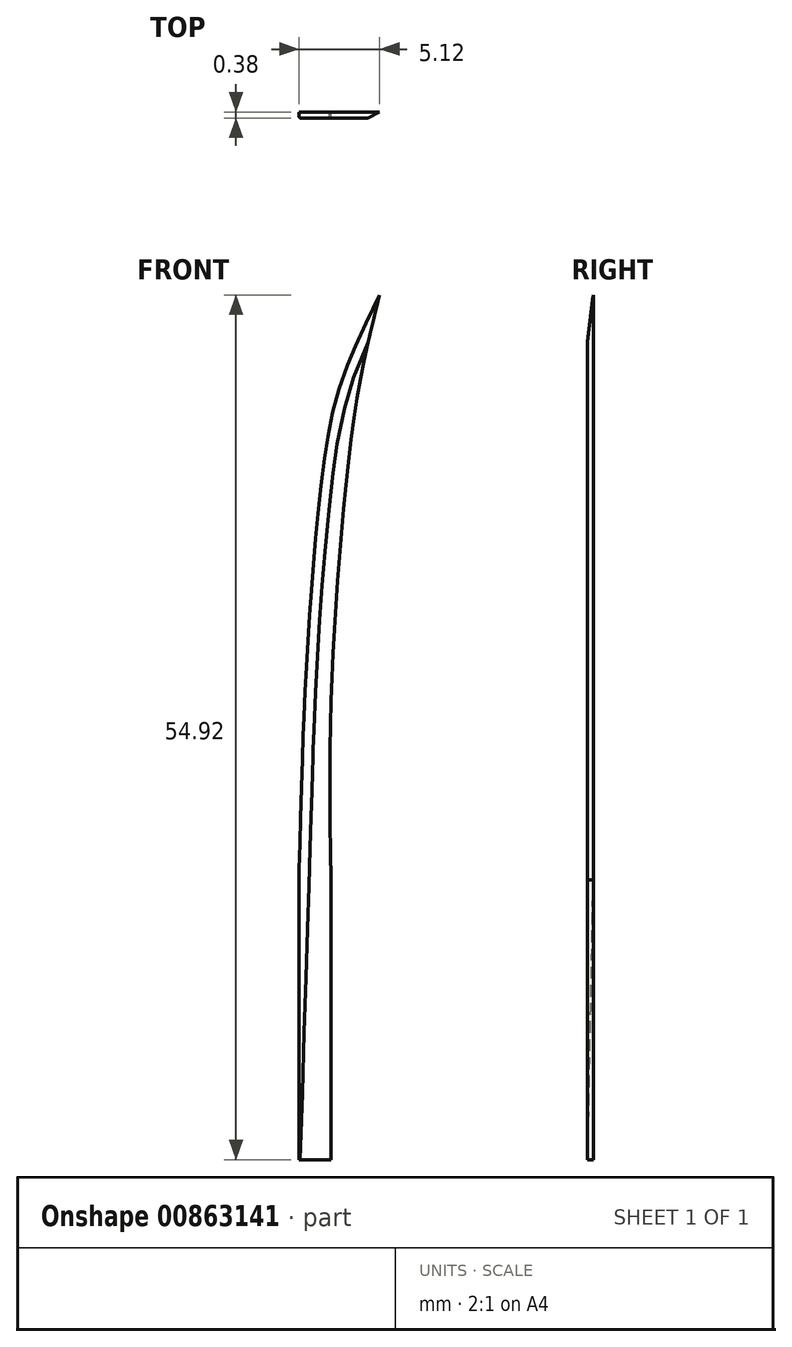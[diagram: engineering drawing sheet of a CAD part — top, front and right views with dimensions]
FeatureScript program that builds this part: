
annotation { "Feature Type Name" : "Feature", "Feature Type Description" : "" }
export const myFeature = defineFeature(function(context is Context, id is Id, definition is map)
    precondition{}
    {
        {
            var Q0;
            Q0=qCreatedBy(makeId("Front.planeOp"),FACE);
            var sketch = newSketch(context, id + "F0", { "sketchPlane" : qUnion([Q0])});
            skLineSegment(sketch, "E0", {"start": v(0, 0) * mm, "end": v(2.03, 0) * mm});
            skLineSegment(sketch, "E1", {"start": v(0, 0) * mm, "end": v(0, 25.4) * mm});
            skLineSegment(sketch, "E2", {"start": v(2.03, 0) * mm, "end": v(2.03, 17.78) * mm});
            skFitSpline(sketch, "E3", {"points": [v(2.03, 17.78) * mm, v(2.03, 29.24) * mm, v(2.67, 39.46) * mm, v(3.7, 48.44) * mm, v(5.36, 55.88) * mm], "startDerivative": vector(-0.98, 47.6) * mm, "endDerivative": vector(10.63, 43.43) * mm});
            skFitSpline(sketch, "E4", {"points": [v(0, 25.4) * mm, v(1.02, 41.31) * mm, v(2.16, 48.44) * mm, v(5.36, 55.88) * mm], "startDerivative": vector(1.39, 44.06) * mm, "endDerivative": vector(17.91, 35.67) * mm});
            skSolve(sketch);
        }
        {
            var Q0;
            Q0=makeQuery(id+"F0.imprint","IMPRINT",FACE,{"disambiguationData":[TD([[makeQuery(id+"F0.imprint","IMPRINT",EDGE,{"derivedFrom":sQuery(id+"F0.wireOp",EDGE,"E0")}),1.0]])]});
            extrude(context, id + "F1", {"entities" : qUnion([Q0]), "depth" : 0.38 * mm, "offsetDistance" : 25.4 * mm});
        }
        {
            var Q0;
            Q0=makeQuery(id+"F1.opExtrude","CAP_EDGE",EDGE,{"disambiguationData":[OSD([sQuery(id+"F0.wireOp",EDGE,"E4")])],"isStart":false});
            chamfer(context, id + "F2", {"entities" : qUnion([Q0]), "chamferType" : ChamferType.OFFSET_ANGLE, "width" : 0.5 * mm, "oppositeDirection" : false, "angle" : 60 * degree, "tangentPropagation" : true});
        }
    });
